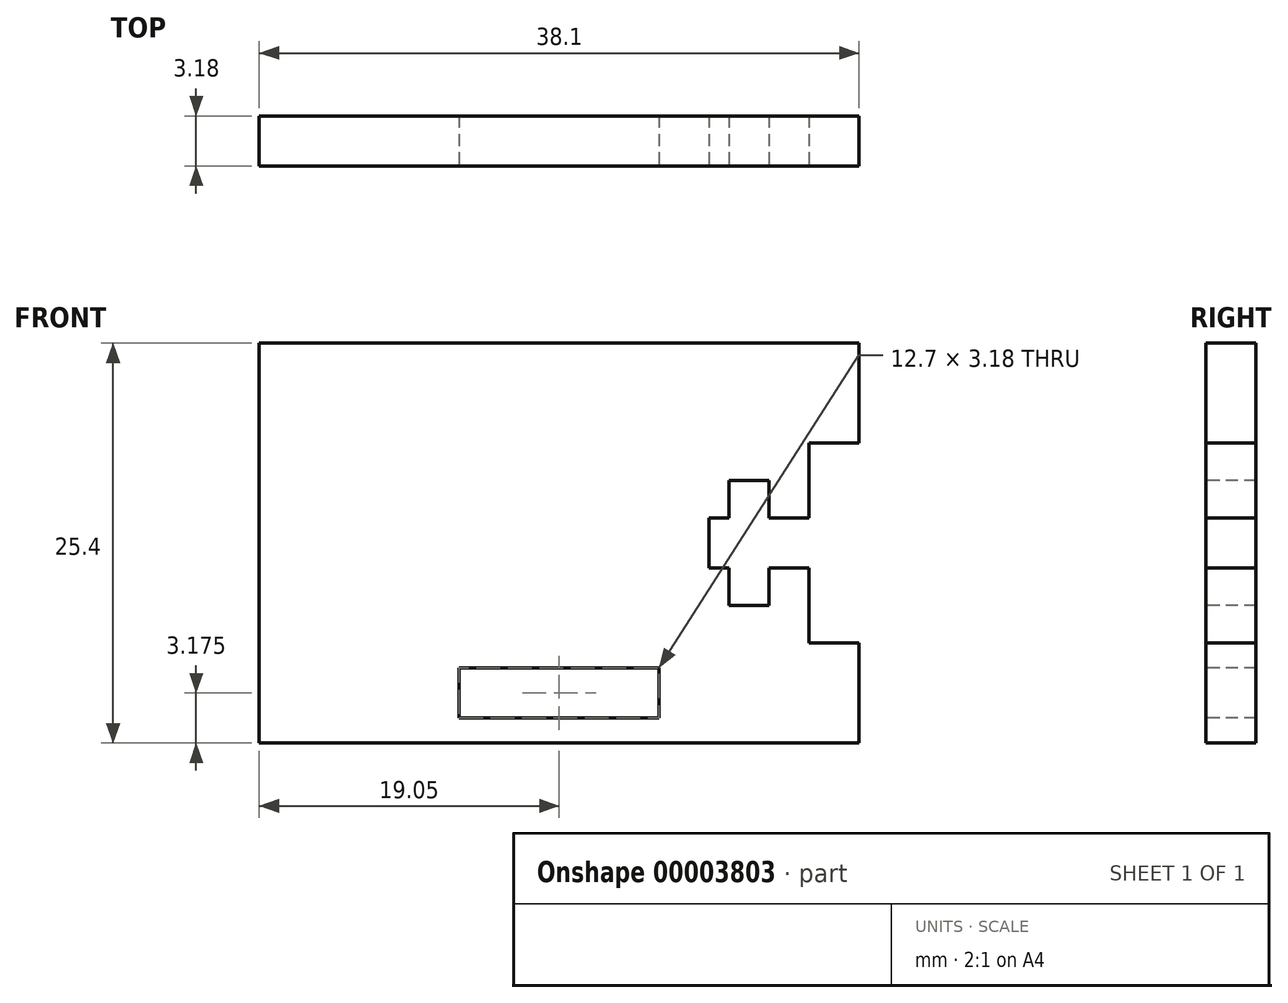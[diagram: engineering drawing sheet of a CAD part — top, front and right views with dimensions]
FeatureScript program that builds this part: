
annotation { "Feature Type Name" : "Feature", "Feature Type Description" : "" }
export const myFeature = defineFeature(function(context is Context, id is Id, definition is map)
    precondition{}
    {
        {
            var Q0;
            Q0=qCreatedBy(makeId("Front.planeOp"),FACE);
            var sketch = newSketch(context, id + "F0", { "sketchPlane" : qUnion([Q0])});
            skLineSegment(sketch, "E0.bottom", {"start": v(0, 0) * mm, "end": v(38.1, 0) * mm});
            skLineSegment(sketch, "E0.top", {"start": v(0, 25.4) * mm, "end": v(38.1, 25.4) * mm});
            skLineSegment(sketch, "E0.left", {"start": v(0, 0) * mm, "end": v(0, 25.4) * mm});
            skLineSegment(sketch, "E0.right", {"start": v(38.1, 0) * mm, "end": v(38.1, 25.4) * mm});
            skSolve(sketch);
        }
        {
            var Q0;
            Q0=makeQuery(id+"F0.imprint","IMPRINT",FACE,{"disambiguationData":[TD([[makeQuery(id+"F0.imprint","IMPRINT",EDGE,{"derivedFrom":sQuery(id+"F0.wireOp",EDGE,"E0.bottom")}),1.0]])]});
            extrude(context, id + "F1", {"entities" : qUnion([Q0]), "oppositeDirection" : true, "depth" : 3.17 * mm});
        }
        {
            var Q0;
            Q0=makeQuery(id+"F1.opExtrude","CAP_FACE",FACE,{"disambiguationData":[OSD([sQuery(id+"F0.wireOp",EDGE,"E0.bottom"),sQuery(id+"F0.wireOp",EDGE,"E0.top"),sQuery(id+"F0.wireOp",EDGE,"E0.left"),sQuery(id+"F0.wireOp",EDGE,"E0.right")])],"isStart":true});
            var sketch = newSketch(context, id + "F2", { "sketchPlane" : qUnion([Q0])});
            skLineSegment(sketch, "E1.bottom", {"start": v(12.7, 1.59) * mm, "end": v(25.4, 1.59) * mm});
            skLineSegment(sketch, "E1.top", {"start": v(12.7, 4.76) * mm, "end": v(25.4, 4.76) * mm});
            skLineSegment(sketch, "E1.left", {"start": v(12.7, 1.59) * mm, "end": v(12.7, 4.76) * mm});
            skLineSegment(sketch, "E1.right", {"start": v(25.4, 1.59) * mm, "end": v(25.4, 4.76) * mm});
            skPoint(sketch, "E2.end.orphan", {"position": v(12.7, 8.08) * mm});
            skSolve(sketch);
        }
        {
            var Q0;
            Q0 = qSketchRegion(id + "F2", true);
            extrude(context, id + "F3", {"entities" : qUnion([Q0]), "operationType" : NewBodyOperationType.REMOVE, "oppositeDirection" : true, "depth" : 40.16 * mm});
        }
        {
            var Q0;
            Q0=makeQuery(id+"F1.opExtrude","CAP_FACE",FACE,{"disambiguationData":[OSD([sQuery(id+"F0.wireOp",EDGE,"E0.bottom"),sQuery(id+"F0.wireOp",EDGE,"E0.top"),sQuery(id+"F0.wireOp",EDGE,"E0.left"),sQuery(id+"F0.wireOp",EDGE,"E0.right")])],"isStart":true});
            var sketch = newSketch(context, id + "F4", { "sketchPlane" : qUnion([Q0])});
            skLineSegment(sketch, "E3.bottom", {"start": v(38.1, 19.05) * mm, "end": v(34.93, 19.05) * mm});
            skLineSegment(sketch, "E3.top", {"start": v(38.1, 6.35) * mm, "end": v(34.93, 6.35) * mm});
            skLineSegment(sketch, "E3.left", {"start": v(38.1, 19.05) * mm, "end": v(38.1, 6.35) * mm});
            skLineSegment(sketch, "E3.right", {"start": v(34.93, 19.05) * mm, "end": v(34.93, 6.35) * mm});
            skLineSegment(sketch, "E4.bottom", {"start": v(38.1, 14.29) * mm, "end": v(28.58, 14.29) * mm});
            skLineSegment(sketch, "E4.top", {"start": v(38.1, 11.11) * mm, "end": v(28.58, 11.11) * mm});
            skLineSegment(sketch, "E4.left", {"start": v(38.1, 14.29) * mm, "end": v(38.1, 11.11) * mm});
            skLineSegment(sketch, "E4.right", {"start": v(28.58, 14.29) * mm, "end": v(28.58, 11.11) * mm});
            skLineSegment(sketch, "E5.bottom", {"start": v(29.85, 16.67) * mm, "end": v(32.39, 16.67) * mm});
            skLineSegment(sketch, "E5.top", {"start": v(29.85, 8.73) * mm, "end": v(32.39, 8.73) * mm});
            skLineSegment(sketch, "E5.left", {"start": v(29.85, 16.67) * mm, "end": v(29.85, 8.73) * mm});
            skLineSegment(sketch, "E5.right", {"start": v(32.39, 16.67) * mm, "end": v(32.39, 8.73) * mm});
            skSolve(sketch);
        }
        {
            var Q0;
            Q0 = qSketchRegion(id + "F4", true);
            extrude(context, id + "F5", {"entities" : qUnion([Q0]), "operationType" : NewBodyOperationType.REMOVE, "oppositeDirection" : true, "depth" : 34.95 * mm});
        }
    });
